FCSTD DOCUMENT  (FreeCAD 0.15R4671 (Git))
Label: ZMotorEnd
License: All rights reserved
LicenseURL: http://en.wikipedia.org/wiki/All_rights_reserved
objects: Sketcher::SketchObject×15, PartDesign::Pocket×12, Part::Feature×8, PartDesign::Fillet×5, PartDesign::Pad×3, PartDesign::Chamfer×3, Mesh::Feature×2
note: 61 computed .brp shape members not serialized (recipe doc carries the construction recipe); baked Part::Feature solids carry a one-line shape summary decoded from their .brp

FEATURE [Mesh::Feature] acoplador_flexivel  label="5x8mmFlexCoupler"
  Placement = pos=(0,-28.14,26) rot=(1,0,0;3.14159rad)
FEATURE [Part::Feature] Part__Feature  label="NEMA_17"
  Placement = pos=(0,-28.14,-7) rot=(0,0,1;3.14159rad)
  shape: bbox 42.3 x 42.3 x 68 mm, 275 faces (baked)
FEATURE [Part::Feature] _mmBrasNut  label="8mmBrassNut"
  Placement = pos=(0,-28.14,59) rot=(0.707107,0,0.707107;3.14159rad)
  shape: bbox 22 x 22 x 16.42 mm, 29 faces (baked)
FEATURE [Part::Feature] _x300mmScrew  label="8x300mmScrew"
  Placement = pos=(0,-28.14,20) rot=(0.707107,0,0.707107;3.14159rad)
  shape: bbox 9.437 x 9.437 x 301.6 mm, 18 faces (baked)
FEATURE [Part::Feature] Part__Feature001  label="8mmRod001"
  Placement = pos=(-60,-28.15,-95) rot=(0,0,1;0rad)
  shape: bbox 8.659 x 8.659 x 420 mm, 5 faces (baked)
FEATURE [Part::Feature] Part__Feature002  label="8mmRod002"
  Placement = pos=(60,-28.15,-95) rot=(0,0,1;0rad)
  shape: bbox 8.659 x 8.659 x 420 mm, 5 faces (baked)
FEATURE [Part::Feature] Part__Feature003  label="OB1515_210mm"
  Placement = pos=(-105,7.5,357.5) rot=(0,1,0;1.5708rad)
  shape: bbox 210 x 15 x 15 mm, 158 faces (baked)
FEATURE [Part::Feature] Part__Feature004  label="OB1515_210mm001"
  Placement = pos=(-105,7.5,-92.5) rot=(0,1,0;1.5708rad)
  shape: bbox 210 x 15 x 15 mm, 158 faces (baked)
FEATURE [Part::Feature] Part__Feature005  label="OB1515_210mm002"
  Placement = pos=(-105,7.5,7.5) rot=(0,1,0;1.5708rad)
  shape: bbox 210 x 15 x 15 mm, 158 faces (baked)
FEATURE [Sketcher::SketchObject] Sketch
  Placement = pos=(0,0,0) rot=(1,0,0;1.5708rad)
  sketch-geometry (9):
    g0: LineSegment StartX=-77.5 StartY=15 StartZ=0 EndX=77.5 EndY=15 EndZ=0
    g1: LineSegment StartX=77.5 StartY=15 StartZ=0 EndX=77.5 EndY=-100 EndZ=0
    g2: LineSegment StartX=77.5 StartY=-100 StartZ=0 EndX=-77.5 EndY=-100 EndZ=0
    g3: LineSegment StartX=-77.5 StartY=-100 StartZ=0 EndX=-77.5 EndY=15 EndZ=0
    g4: Circle CenterX=72.5 CenterY=7.5 CenterZ=0 NormalX=0 NormalY=0 NormalZ=1 Radius=1.8
    g5: Circle CenterX=72.5 CenterY=-92.5 CenterZ=0 NormalX=0 NormalY=0 NormalZ=1 Radius=1.8
    g6: Circle CenterX=-72.5 CenterY=-92.5 CenterZ=0 NormalX=0 NormalY=0 NormalZ=1 Radius=1.8
    g7: Circle CenterX=-72.5 CenterY=7.5 CenterZ=0 NormalX=0 NormalY=0 NormalZ=1 Radius=1.8
    g8: Circle CenterX=0 CenterY=7.5 CenterZ=0 NormalX=0 NormalY=0 NormalZ=1 Radius=1.8
  constraints (17):
    c: Coincident(g0,g1)
    c: Coincident(g1,g2)
    c: Coincident(g2,g3)
    c: Coincident(g3,g0)
    c: Horizontal(g0)
    c: Horizontal(g2)
    c: Vertical(g1)
    c: Vertical(g3)
    c: DistanceY(g0,g2) = -115
    c: Radius(g7) = 1.8
    c: Equal(g7,g4)
    c: Equal(g7,g5)
    c: Equal(g7,g6)
    c: DistanceX(g1,g2) = -155
    c: DistanceX(g0) = -77.5
    c: DistanceY(g0) = 15
    c: Radius(g8) = 1.8
FEATURE [PartDesign::Pad] Pad
  Length = 7
  Length2 = 100
  Placement = pos=(0,0,0) rot=(1,0,0;1.5708rad)
  Sketch = -> Sketch
  Type = 0
FEATURE [Sketcher::SketchObject] Sketch001
  Placement = pos=(0,-7,0) rot=(1,0,0;1.5708rad)
  Support = -> Pad [Face11]
  sketch-geometry (8):
    g0: LineSegment StartX=24 StartY=-7 StartZ=0 EndX=-24 EndY=-7 EndZ=0
    g1: LineSegment StartX=-24 StartY=-7 StartZ=0 EndX=-24 EndY=-53 EndZ=0
    g2: LineSegment StartX=-24 StartY=-53 StartZ=0 EndX=-27 EndY=-53 EndZ=0
    g3: LineSegment StartX=-27 StartY=-53 StartZ=0 EndX=-27 EndY=0 EndZ=0
    g4: LineSegment StartX=-27 StartY=0 StartZ=0 EndX=27 EndY=0 EndZ=0
    g5: LineSegment StartX=27 StartY=0 StartZ=0 EndX=27 EndY=-53 EndZ=0
    g6: LineSegment StartX=27 StartY=-53 StartZ=0 EndX=24 EndY=-53 EndZ=0
    g7: LineSegment StartX=24 StartY=-53 StartZ=0 EndX=24 EndY=-7 EndZ=0
  constraints (17):
    c: Horizontal(g0)
    c: Coincident(g0,g1)
    c: Vertical(g1)
    c: Coincident(g1,g2)
    c: Horizontal(g2)
    c: Coincident(g2,g3)
    c: Vertical(g3)
    c: Coincident(g3,g4)
    c: PointOnObject(g4,g-1)
    c: Horizontal(g4)
    c: Coincident(g4,g5)
    c: Vertical(g5)
    c: Coincident(g5,g6)
    c: Horizontal(g6)
    c: Coincident(g6,g7)
    c: Coincident(g7,g0)
    c: Vertical(g7)
FEATURE [PartDesign::Pad] Pad001
  Length = 42.5
  Length2 = 100
  Placement = pos=(0,0,0) rot=(1,0,0;1.5708rad)
  Sketch = -> Sketch001
  Type = 0
FEATURE [Sketcher::SketchObject] Sketch002
  Placement = pos=(0,-7,0) rot=(1,0,0;1.5708rad)
  Support = -> Pad001 [Face5]
  sketch-geometry (4):
    g0: LineSegment StartX=-24 StartY=-7 StartZ=0 EndX=24 EndY=-7 EndZ=0
    g1: LineSegment StartX=24 StartY=-7 StartZ=0 EndX=24 EndY=-53 EndZ=0
    g2: LineSegment StartX=24 StartY=-53 StartZ=0 EndX=-24 EndY=-53 EndZ=0
    g3: LineSegment StartX=-24 StartY=-53 StartZ=0 EndX=-24 EndY=-7 EndZ=0
  constraints (8):
    c: Coincident(g0,g1)
    c: Coincident(g1,g2)
    c: Coincident(g2,g3)
    c: Coincident(g3,g0)
    c: Horizontal(g0)
    c: Horizontal(g2)
    c: Vertical(g1)
    c: Vertical(g3)
FEATURE [PartDesign::Pocket] Pocket
  Length = 2
  Placement = pos=(0,0,0) rot=(1,0,0;1.5708rad)
  Sketch = -> Sketch002
  Type = 0
FEATURE [Sketcher::SketchObject] Sketch004
  Placement = pos=(27,0,0) rot=(0.707107,0,0.707107;3.14159rad)
  Support = -> Pocket [Face14]
  sketch-geometry (5):
    g0: LineSegment StartX=-55 StartY=7 StartZ=0 EndX=-53 EndY=7 EndZ=0
    g1: LineSegment StartX=-53 StartY=7 StartZ=0 EndX=-7 EndY=49.5 EndZ=0
    g2: LineSegment StartX=-7 StartY=49.5 StartZ=0 EndX=-7 EndY=52 EndZ=0
    g3: LineSegment StartX=-7 StartY=52 StartZ=0 EndX=-55 EndY=52 EndZ=0
    g4: LineSegment StartX=-55 StartY=52 StartZ=0 EndX=-55 EndY=7 EndZ=0
  constraints (8):
    c: Horizontal(g0)
    c: Coincident(g0,g1)
    c: Coincident(g1,g2)
    c: Coincident(g2,g3)
    c: Horizontal(g3)
    c: Coincident(g3,g4)
    c: Coincident(g4,g0)
    c: Vertical(g4)
FEATURE [PartDesign::Pocket] Pocket001
  Length = 5
  Placement = pos=(0,0,0) rot=(1,0,0;1.5708rad)
  Sketch = -> Sketch004
  Type = 1
FEATURE [Sketcher::SketchObject] Sketch005
  Placement = pos=(0,0,0) rot=(0,0,1;3.14159rad)
  Support = -> Pocket001 [Face15]
  sketch-geometry (5):
    g0: Circle CenterX=-15.5 CenterY=43.6552 CenterZ=0 NormalX=0 NormalY=0 NormalZ=1 Radius=1.8
    g1: Circle CenterX=15.5 CenterY=43.6605 CenterZ=0 NormalX=0 NormalY=0 NormalZ=1 Radius=1.8
    g2: Circle CenterX=15.5 CenterY=12.6629 CenterZ=0 NormalX=0 NormalY=0 NormalZ=1 Radius=1.8
    g3: Circle CenterX=-15.5 CenterY=12.6615 CenterZ=0 NormalX=0 NormalY=0 NormalZ=1 Radius=1.8
    g4: Circle CenterX=0 CenterY=28.1466 CenterZ=0 NormalX=0 NormalY=0 NormalZ=1 Radius=12
  constraints (6):
    c: PointOnObject(g4,g-2)
    c: Radius(g0) = 1.8
    c: Equal(g0,g1)
    c: Equal(g0,g2)
    c: Equal(g0,g3)
    c: Radius(g4) = 12
FEATURE [PartDesign::Pocket] Pocket002
  Length = 5
  Placement = pos=(0,0,0) rot=(1,0,0;1.5708rad)
  Sketch = -> Sketch005
  Type = 1
FEATURE [Sketcher::SketchObject] Sketch006
  Placement = pos=(0,0,0) rot=(0,0,1;3.14159rad)
  Support = -> Pocket002 [Face17]
  sketch-geometry (4):
    g0: Circle CenterX=-15.5 CenterY=43.6727 CenterZ=0 NormalX=0 NormalY=0 NormalZ=1 Radius=3.6
    g1: Circle CenterX=15.5 CenterY=43.6745 CenterZ=0 NormalX=0 NormalY=0 NormalZ=1 Radius=3.6
    g2: Circle CenterX=15.5 CenterY=12.6769 CenterZ=0 NormalX=0 NormalY=0 NormalZ=1 Radius=3.6
    g3: Circle CenterX=-15.5 CenterY=12.6477 CenterZ=0 NormalX=0 NormalY=0 NormalZ=1 Radius=3.6
  constraints (4):
    c: Radius(g0) = 3.6
    c: Equal(g0,g1)
    c: Equal(g0,g2)
    c: Equal(g0,g3)
FEATURE [PartDesign::Pocket] Pocket003
  Length = 3
  Placement = pos=(0,0,0) rot=(1,0,0;1.5708rad)
  Sketch = -> Sketch006
  Type = 0
FEATURE [PartDesign::Fillet] Fillet
  Base = -> Pocket003 [Edge37,Edge48]
  Placement = pos=(0,0,0) rot=(1,0,0;1.5708rad)
  Radius = 2
FEATURE [Sketcher::SketchObject] Sketch007
  Placement = pos=(0,-7,0) rot=(1,0,0;1.5708rad)
  Support = -> Fillet [Face4]
  sketch-geometry (5):
    g0: Circle CenterX=-72.5 CenterY=7.5 CenterZ=0 NormalX=0 NormalY=0 NormalZ=1 Radius=3.6
    g1: Circle CenterX=0 CenterY=7.5 CenterZ=0 NormalX=0 NormalY=0 NormalZ=1 Radius=3.6
    g2: Circle CenterX=72.5 CenterY=7.5 CenterZ=0 NormalX=0 NormalY=0 NormalZ=1 Radius=3.6
    g3: Circle CenterX=72.5 CenterY=-92.5 CenterZ=0 NormalX=0 NormalY=0 NormalZ=1 Radius=3.6
    g4: Circle CenterX=-72.5 CenterY=-92.5 CenterZ=0 NormalX=0 NormalY=0 NormalZ=1 Radius=3.6
  constraints (3):
    c: PointOnObject(g1,g-2)
    c: Radius(g0) = 3.6
    c: Equal(g0, g1-g4) x4
FEATURE [PartDesign::Pocket] Pocket004
  Length = 3
  Placement = pos=(0,0,0) rot=(1,0,0;1.5708rad)
  Sketch = -> Sketch007
  Type = 0
FEATURE [Sketcher::SketchObject] Sketch008
  Placement = pos=(0,-7,0) rot=(1,0,0;1.5708rad)
  Support = -> Pocket004 [Face4]
  sketch-geometry (16):
    g0: LineSegment StartX=-68 StartY=15 StartZ=0 EndX=-52 EndY=15 EndZ=0
    g1: LineSegment StartX=-52 StartY=15 StartZ=0 EndX=-52 EndY=-5 EndZ=0
    g2: LineSegment StartX=-52 StartY=-5 StartZ=0 EndX=-68 EndY=-5 EndZ=0
    g3: LineSegment StartX=-68 StartY=-5 StartZ=0 EndX=-68 EndY=15 EndZ=0
    g4: LineSegment StartX=52 StartY=15 StartZ=0 EndX=68 EndY=15 EndZ=0
    g5: LineSegment StartX=68 StartY=15 StartZ=0 EndX=68 EndY=-5 EndZ=0
    g6: LineSegment StartX=68 StartY=-5 StartZ=0 EndX=52 EndY=-5 EndZ=0
    g7: LineSegment StartX=52 StartY=-5 StartZ=0 EndX=52 EndY=15 EndZ=0
    g8: LineSegment StartX=-68 StartY=-100 StartZ=0 EndX=-52 EndY=-100 EndZ=0
    g9: LineSegment StartX=-52 StartY=-100 StartZ=0 EndX=-52 EndY=-80 EndZ=0
    g10: LineSegment StartX=-52 StartY=-80 StartZ=0 EndX=-68 EndY=-80 EndZ=0
    g11: LineSegment StartX=-68 StartY=-80 StartZ=0 EndX=-68 EndY=-100 EndZ=0
    g12: LineSegment StartX=52 StartY=-100 StartZ=0 EndX=68 EndY=-100 EndZ=0
    g13: LineSegment StartX=68 StartY=-100 StartZ=0 EndX=68 EndY=-80 EndZ=0
    g14: LineSegment StartX=68 StartY=-80 StartZ=0 EndX=52 EndY=-80 EndZ=0
    g15: LineSegment StartX=52 StartY=-80 StartZ=0 EndX=52 EndY=-100 EndZ=0
  constraints (32):
    c: Coincident(g0,g1)
    c: Coincident(g1,g2)
    c: Coincident(g2,g3)
    c: Coincident(g3,g0)
    c: Horizontal(g0)
    c: Horizontal(g2)
    c: Vertical(g1)
    c: Vertical(g3)
    c: Coincident(g4,g5)
    c: Coincident(g5,g6)
    c: Coincident(g6,g7)
    c: Coincident(g7,g4)
    c: Horizontal(g4)
    c: Horizontal(g6)
    c: Vertical(g5)
    c: Vertical(g7)
    c: Coincident(g8,g9)
    c: Coincident(g9,g10)
    c: Coincident(g10,g11)
    c: Coincident(g11,g8)
    c: Horizontal(g8)
    c: Horizontal(g10)
    c: Vertical(g9)
    c: Vertical(g11)
    c: Coincident(g12,g13)
    c: Coincident(g13,g14)
    c: Coincident(g14,g15)
    c: Coincident(g15,g12)
    c: Horizontal(g12)
    c: Horizontal(g14)
    c: Vertical(g13)
    c: Vertical(g15)
FEATURE [PartDesign::Pad] Pad002
  Length = 29
  Length2 = 100
  Placement = pos=(0,0,0) rot=(1,0,0;1.5708rad)
  Sketch = -> Sketch008
  Type = 0
FEATURE [PartDesign::Fillet] Fillet001
  Base = -> Pad002 [Edge75,Edge70,Edge65,Edge79,Edge63,Edge58,Edge82,Edge86]
  Placement = pos=(0,0,0) rot=(1,0,0;1.5708rad)
  Radius = 7.99
FEATURE [PartDesign::Chamfer] Chamfer
  Base = -> Fillet001 [Edge25,Edge13,Edge15,Edge23]
  Placement = pos=(0,0,0) rot=(1,0,0;1.5708rad)
  Size = 20
FEATURE [Sketcher::SketchObject] Sketch009
  Placement = pos=(0,-7,0) rot=(1,0,0;1.5708rad)
  Support = -> Chamfer [Face5]
  sketch-geometry (16):
    g0: LineSegment StartX=-79 StartY=0 StartZ=0 EndX=-68 EndY=0 EndZ=0
    g1: LineSegment StartX=-68 StartY=0 StartZ=0 EndX=-68 EndY=-5 EndZ=0
    g2: LineSegment StartX=-68 StartY=-5 StartZ=0 EndX=-27 EndY=-5 EndZ=0
    g3: LineSegment StartX=-27 StartY=-5 StartZ=0 EndX=-27 EndY=-53 EndZ=0
    g4: LineSegment StartX=-27 StartY=-53 StartZ=0 EndX=27 EndY=-53 EndZ=0
    g5: LineSegment StartX=27 StartY=-53 StartZ=0 EndX=27 EndY=-5 EndZ=0
    g6: LineSegment StartX=27 StartY=-5 StartZ=0 EndX=68 EndY=-5 EndZ=0
    g7: LineSegment StartX=68 StartY=-5 StartZ=0 EndX=68 EndY=0 EndZ=0
    g8: LineSegment StartX=68 StartY=0 StartZ=0 EndX=79.6841 EndY=0 EndZ=0
    g9: LineSegment StartX=79.6841 StartY=0 StartZ=0 EndX=79.6841 EndY=-85 EndZ=0
    g10: LineSegment StartX=79.6841 StartY=-85 StartZ=0 EndX=68 EndY=-85 EndZ=0
    g11: LineSegment StartX=68 StartY=-85 StartZ=0 EndX=68 EndY=-80 EndZ=0
    g12: LineSegment StartX=68 StartY=-80 StartZ=0 EndX=-68 EndY=-80 EndZ=0
    g13: LineSegment StartX=-68 StartY=-80 StartZ=0 EndX=-68 EndY=-85 EndZ=0
    g14: LineSegment StartX=-68 StartY=-85 StartZ=0 EndX=-79 EndY=-85 EndZ=0
    g15: LineSegment StartX=-79 StartY=-85 StartZ=0 EndX=-79 EndY=0 EndZ=0
  constraints (33):
    c: PointOnObject(g0,g-1)
    c: PointOnObject(g0,g-1)
    c: Coincident(g0,g1)
    c: Vertical(g1)
    c: Coincident(g1,g2)
    c: Horizontal(g2)
    c: Coincident(g2,g3)
    c: Vertical(g3)
    c: Coincident(g3,g4)
    c: Horizontal(g4)
    c: Coincident(g4,g5)
    c: Vertical(g5)
    c: Coincident(g5,g6)
    c: Horizontal(g6)
    c: Coincident(g6,g7)
    c: PointOnObject(g7,g-1)
    c: Coincident(g7,g8)
    c: PointOnObject(g8,g-1)
    c: Coincident(g8,g9)
    c: Vertical(g9)
    c: Coincident(g9,g10)
    c: Horizontal(g10)
    c: Coincident(g10,g11)
    c: Vertical(g11)
    c: Coincident(g11,g12)
    c: Horizontal(g12)
    c: Coincident(g12,g13)
    c: Vertical(g13)
    c: Coincident(g13,g14)
    c: Horizontal(g14)
    c: Coincident(g14,g15)
    c: Coincident(g15,g0)
    c: Vertical(g15)
FEATURE [PartDesign::Pocket] Pocket005
  Length = 4
  Placement = pos=(0,0,0) rot=(1,0,0;1.5708rad)
  Sketch = -> Sketch009
  Type = 0
FEATURE [PartDesign::Fillet] Fillet002
  Base = -> Pocket005 [Edge28,Edge82,Edge24,Edge54]
  Placement = pos=(0,0,0) rot=(1,0,0;1.5708rad)
  Radius = 4
FEATURE [Sketcher::SketchObject] Sketch010
  Placement = pos=(0,0,15) rot=(0,0,1;3.14159rad)
  Support = -> Fillet002 [Face1]
  sketch-geometry (2):
    g0: Circle CenterX=-60 CenterY=28.1364 CenterZ=0 NormalX=0 NormalY=0 NormalZ=1 Radius=4.3
    g1: Circle CenterX=60 CenterY=28.1455 CenterZ=0 NormalX=0 NormalY=0 NormalZ=1 Radius=4.3
  constraints (2):
    c: Radius(g0) = 4.3
    c: Equal(g0,g1)
FEATURE [PartDesign::Pocket] Pocket006
  Length = 30
  Placement = pos=(0,0,0) rot=(1,0,0;1.5708rad)
  Sketch = -> Sketch010
  Type = 0
FEATURE [Sketcher::SketchObject] Sketch011
  Placement = pos=(0,0,-80) rot=(0,0,1;3.14159rad)
  Support = -> Pocket006 [Face49]
  sketch-geometry (2):
    g0: Circle CenterX=-60 CenterY=28.1606 CenterZ=0 NormalX=0 NormalY=0 NormalZ=1 Radius=4.3
    g1: Circle CenterX=60 CenterY=28.1499 CenterZ=0 NormalX=0 NormalY=0 NormalZ=1 Radius=4.3
  constraints (2):
    c: Radius(g0) = 4.3
    c: Equal(g0,g1)
FEATURE [PartDesign::Pocket] Pocket007
  Length = 15
  Placement = pos=(0,0,0) rot=(1,0,0;1.5708rad)
  Sketch = -> Sketch011
  Type = 0
FEATURE [Mesh::Feature] MicroSwitch
  Placement = pos=(75,-18,10) rot=(0.57735,-0.57735,-0.57735;2.0944rad)
FEATURE [Sketcher::SketchObject] Sketch012
  Placement = pos=(68,0,0) rot=(0.707107,0,0.707107;3.14159rad)
  Support = -> Pocket007 [Face11]
  sketch-geometry (2):
    g0: Circle CenterX=7.25 CenterY=23 CenterZ=0 NormalX=0 NormalY=0 NormalZ=1 Radius=1
    g1: Circle CenterX=7.25 CenterY=13.4456 CenterZ=0 NormalX=0 NormalY=0 NormalZ=1 Radius=1
  constraints (2):
    c: Radius(g1) = 1
    c: Equal(g1,g0)
FEATURE [PartDesign::Pocket] Pocket008
  Length = 5
  Placement = pos=(0,0,0) rot=(1,0,0;1.5708rad)
  Sketch = -> Sketch012
  Type = 0
FEATURE [Sketcher::SketchObject] Sketch013
  Placement = pos=(0,-3,0) rot=(1,0,0;1.5708rad)
  Support = -> Pocket008 [Face26]
  sketch-geometry (8):
    g0: LineSegment StartX=-82 StartY=-5 StartZ=0 EndX=-32 EndY=-5 EndZ=0
    g1: LineSegment StartX=-32 StartY=-5 StartZ=0 EndX=-32 EndY=-80 EndZ=0
    g2: LineSegment StartX=-32 StartY=-80 StartZ=0 EndX=-82 EndY=-80 EndZ=0
    g3: LineSegment StartX=-82 StartY=-80 StartZ=0 EndX=-82 EndY=-5 EndZ=0
    g4: LineSegment StartX=32 StartY=-5 StartZ=0 EndX=82.2293 EndY=-5 EndZ=0
    g5: LineSegment StartX=82.2293 StartY=-5 StartZ=0 EndX=82.2293 EndY=-80 EndZ=0
    g6: LineSegment StartX=82.2293 StartY=-80 StartZ=0 EndX=32 EndY=-80 EndZ=0
    g7: LineSegment StartX=32 StartY=-80 StartZ=0 EndX=32 EndY=-5 EndZ=0
  constraints (16):
    c: Coincident(g0,g1)
    c: Coincident(g1,g2)
    c: Coincident(g2,g3)
    c: Coincident(g3,g0)
    c: Horizontal(g0)
    c: Horizontal(g2)
    c: Vertical(g1)
    c: Vertical(g3)
    c: Coincident(g4,g5)
    c: Coincident(g5,g6)
    c: Coincident(g6,g7)
    c: Coincident(g7,g4)
    c: Horizontal(g4)
    c: Horizontal(g6)
    c: Vertical(g5)
    c: Vertical(g7)
FEATURE [PartDesign::Pocket] Pocket009
  Length = 5
  Placement = pos=(0,0,0) rot=(1,0,0;1.5708rad)
  Sketch = -> Sketch013
  Type = 0
FEATURE [Sketcher::SketchObject] Sketch014
  Placement = pos=(0,-3,0) rot=(1,0,0;1.5708rad)
  Support = -> Pocket009 [Face50]
  sketch-geometry (16):
    g0: LineSegment StartX=68 StartY=-78 StartZ=0 EndX=80 EndY=-78 EndZ=0
    g1: LineSegment StartX=80 StartY=-78 StartZ=0 EndX=80 EndY=-85 EndZ=0
    g2: LineSegment StartX=80 StartY=-85 StartZ=0 EndX=68 EndY=-85 EndZ=0
    g3: LineSegment StartX=68 StartY=-85 StartZ=0 EndX=68 EndY=-78 EndZ=0
    g4: LineSegment StartX=-79 StartY=-78 StartZ=0 EndX=-68 EndY=-78 EndZ=0
    g5: LineSegment StartX=-68 StartY=-78 StartZ=0 EndX=-68 EndY=-85 EndZ=0
    g6: LineSegment StartX=-68 StartY=-85 StartZ=0 EndX=-79 EndY=-85 EndZ=0
    g7: LineSegment StartX=-79 StartY=-85 StartZ=0 EndX=-79 EndY=-78 EndZ=0
    g8: LineSegment StartX=-79 StartY=0 StartZ=0 EndX=-68 EndY=0 EndZ=0
    g9: LineSegment StartX=-68 StartY=0 StartZ=0 EndX=-68 EndY=-7 EndZ=0
    g10: LineSegment StartX=-68 StartY=-7 StartZ=0 EndX=-79 EndY=-7 EndZ=0
    g11: LineSegment StartX=-79 StartY=-7 StartZ=0 EndX=-79 EndY=0 EndZ=0
    g12: LineSegment StartX=79 StartY=-7 StartZ=0 EndX=68 EndY=-7 EndZ=0
    g13: LineSegment StartX=68 StartY=-7 StartZ=0 EndX=68 EndY=0 EndZ=0
    g14: LineSegment StartX=68 StartY=0 StartZ=0 EndX=79 EndY=0 EndZ=0
    g15: LineSegment StartX=79 StartY=0 StartZ=0 EndX=79 EndY=-7 EndZ=0
  constraints (34):
    c: Coincident(g0,g1)
    c: Coincident(g1,g2)
    c: Coincident(g2,g3)
    c: Coincident(g3,g0)
    c: Horizontal(g0)
    c: Horizontal(g2)
    c: Vertical(g1)
    c: Vertical(g3)
    c: Coincident(g4,g5)
    c: Coincident(g5,g6)
    c: Coincident(g6,g7)
    c: Coincident(g7,g4)
    c: Horizontal(g4)
    c: Horizontal(g6)
    c: Vertical(g5)
    c: Vertical(g7)
    c: Coincident(g8,g9)
    c: Coincident(g9,g10)
    c: Coincident(g10,g11)
    c: Coincident(g11,g8)
    c: Horizontal(g8)
    c: Horizontal(g10)
    c: Vertical(g9)
    c: Vertical(g11)
    c: PointOnObject(g8,g-1)
    c: Coincident(g12,g13)
    c: Coincident(g13,g14)
    c: Coincident(g14,g15)
    c: Coincident(g15,g12)
    c: Horizontal(g12)
    c: Horizontal(g14)
    c: Vertical(g13)
    c: Vertical(g15)
    c: PointOnObject(g13,g-1)
FEATURE [PartDesign::Pocket] Pocket010
  Length = 5
  Placement = pos=(0,0,0) rot=(1,0,0;1.5708rad)
  Sketch = -> Sketch014
  Type = 1
FEATURE [PartDesign::Fillet] Fillet003
  Base = -> Pocket010 [Edge103]
  Placement = pos=(0,0,0) rot=(1,0,0;1.5708rad)
  Radius = 4
FEATURE [Sketcher::SketchObject] Sketch015
  Placement = pos=(0,-3,0) rot=(1,0,0;1.5708rad)
  Support = -> Fillet003 [Face50]
  sketch-geometry (8):
    g0: LineSegment StartX=-34 StartY=-5 StartZ=0 EndX=-27 EndY=-5 EndZ=0
    g1: LineSegment StartX=-27 StartY=-5 StartZ=0 EndX=-27 EndY=-80 EndZ=0
    g2: LineSegment StartX=-27 StartY=-80 StartZ=0 EndX=-34 EndY=-80 EndZ=0
    g3: LineSegment StartX=-34 StartY=-80 StartZ=0 EndX=-34 EndY=-5 EndZ=0
    g4: LineSegment StartX=34 StartY=-5 StartZ=0 EndX=27 EndY=-5 EndZ=0
    g5: LineSegment StartX=27 StartY=-5 StartZ=0 EndX=27 EndY=-80 EndZ=0
    g6: LineSegment StartX=27 StartY=-80 StartZ=0 EndX=34 EndY=-80 EndZ=0
    g7: LineSegment StartX=34 StartY=-80 StartZ=0 EndX=34 EndY=-5 EndZ=0
  constraints (16):
    c: Coincident(g0,g1)
    c: Coincident(g1,g2)
    c: Coincident(g2,g3)
    c: Coincident(g3,g0)
    c: Horizontal(g0)
    c: Horizontal(g2)
    c: Vertical(g1)
    c: Vertical(g3)
    c: Coincident(g4,g5)
    c: Coincident(g5,g6)
    c: Coincident(g6,g7)
    c: Coincident(g7,g4)
    c: Horizontal(g4)
    c: Horizontal(g6)
    c: Vertical(g5)
    c: Vertical(g7)
FEATURE [PartDesign::Pocket] Pocket011
  Length = 5
  Placement = pos=(0,0,0) rot=(1,0,0;1.5708rad)
  Sketch = -> Sketch015
  Type = 0
FEATURE [PartDesign::Chamfer] Chamfer001
  Base = -> Pocket011 [Edge226]
  Placement = pos=(0,0,0) rot=(1,0,0;1.5708rad)
  Size = 1.99
FEATURE [PartDesign::Chamfer] Chamfer002
  Base = -> Chamfer001 [Edge33]
  Placement = pos=(0,0,0) rot=(1,0,0;1.5708rad)
  Size = 3.99
FEATURE [PartDesign::Fillet] Fillet004  label="TempZMotorEnd"
  Base = -> Chamfer002 [Edge21,Edge24]
  Placement = pos=(0,0,0) rot=(1,0,0;1.5708rad)
  Radius = 4
